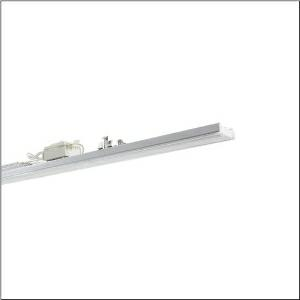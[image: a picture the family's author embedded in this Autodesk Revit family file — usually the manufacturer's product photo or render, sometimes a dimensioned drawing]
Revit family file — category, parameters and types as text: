
# Revit family: licross_21_recessed_ho_52tl12dv4lxm
name_source: partatom
category: Lighting Fixtures
units: mm (PartAtom-declared; Revit-internal decimal feet)

## family parameters
Cut with Voids When Loaded = No
Host = Face
Light Source = No
Part Type = Normal
Room Calculation Point = No
Round Connector Dimension = Use Diameter
Shared = No

## types (1)
- --- (1 x LED, 20000 lm, 109.8 W, 4000K)
    Apparent Load = 110 VA
    CIE Flux Codes = 69 91 98 100 100
    Color Rendering = 80
    Color Temperature = 4000K
    Default Elevation = 1800 mm
    Description = Licross 21 Recessed HO, luminaire insert, of sheet steel, galvanised, coil coated, white, length: 2.250mm, width: 66mm, height: 67mm, LED rated luminous flux: 20.000lm, light colour: 840, SDCM (Standard Deviation of Colour Matching)MacAdam ≤ 3 SDCM (initial), control gear: DALI 2, with plug, 5-pole, with phase selection, mains connection: 220..240V, AC, 50/60Hz, rated input power: 110W, internal wiring halogen-free, primary optical cover: cover, of PMMA, light emission: direct distribution, primary light characteristic: symmetric, protection rating (complete): IP40, insulation class (complete): insulation class I (protective earthing), certification: CE, ENEC, VDE, UKCA, protection symbol: D if used in an environment without relevant dust loads with corresponding accessories, impact resistance: IK06, permissible ambient temperature for indoor applications: -40..+35°C, corresponds to IFS (International Featured Standards) requirements for safety and quality in the food industry, reducing of maximum allowable ambient temperature of 5°C with ceiling mounting, LABS conformity tested according to VDMA 24364:2018-05, The light source and the operating device comply with the requirements of the Ecodesign Regulation (EU) 2019/2020 and are replaceable in accordance with this regulation, packaging unit: 1 piece
    Height = 58 mm
    Lamp = 1 x LED
    Lamp Light Flux = 20000 lm
    Lamp Power = 109.8 W
    Lamp count = 1
    Length = 2250 mm
    Luminous efficacy = 182 lm/W
    Manufacturer = Siteco
    ModVariant = No
    Model = 52TL12DV4LXM
    Mounting Place = Ceiling
    Mounting Type = Pendant
    Number of Poles = 1
    OnlyDefault = Yes
    Power Factor = 1
    Product Name = Licross 21 Recessed HO
    Product group = luminaire insert | ceiling pendant
    ProductGroupID = 901
    Protection Class = Protection class I
    Protection Degree = IP 40
    RLX_Detail_Level = 1
    RLX_Emergency_Light_Flux = 0 lm
    RLX_Emergency_Type = 0
    RLX_Emergency_Type_DB = No
    RlxData = <blob elided: 29661 chars, md5=6741b560>
    Socket = socket
    Standby Power = 0 W
    System Light Flux = 20000 lm
    System Power = 110 W
    Type Comments = factory setting: luminous flux: 100 % | dim-lin: 254 | 425 mA
    Type Image = l_1296930.jpg
    URL = http://relux.com
    VarID = @adj_116851
    Voltage = 0 V
    Weight = 0.00 kg
    Width = 66 mm

## geometry (parser evidence)
native form markers: Blend x4, Sweep x11
no freeform markers — native parametric forms only
